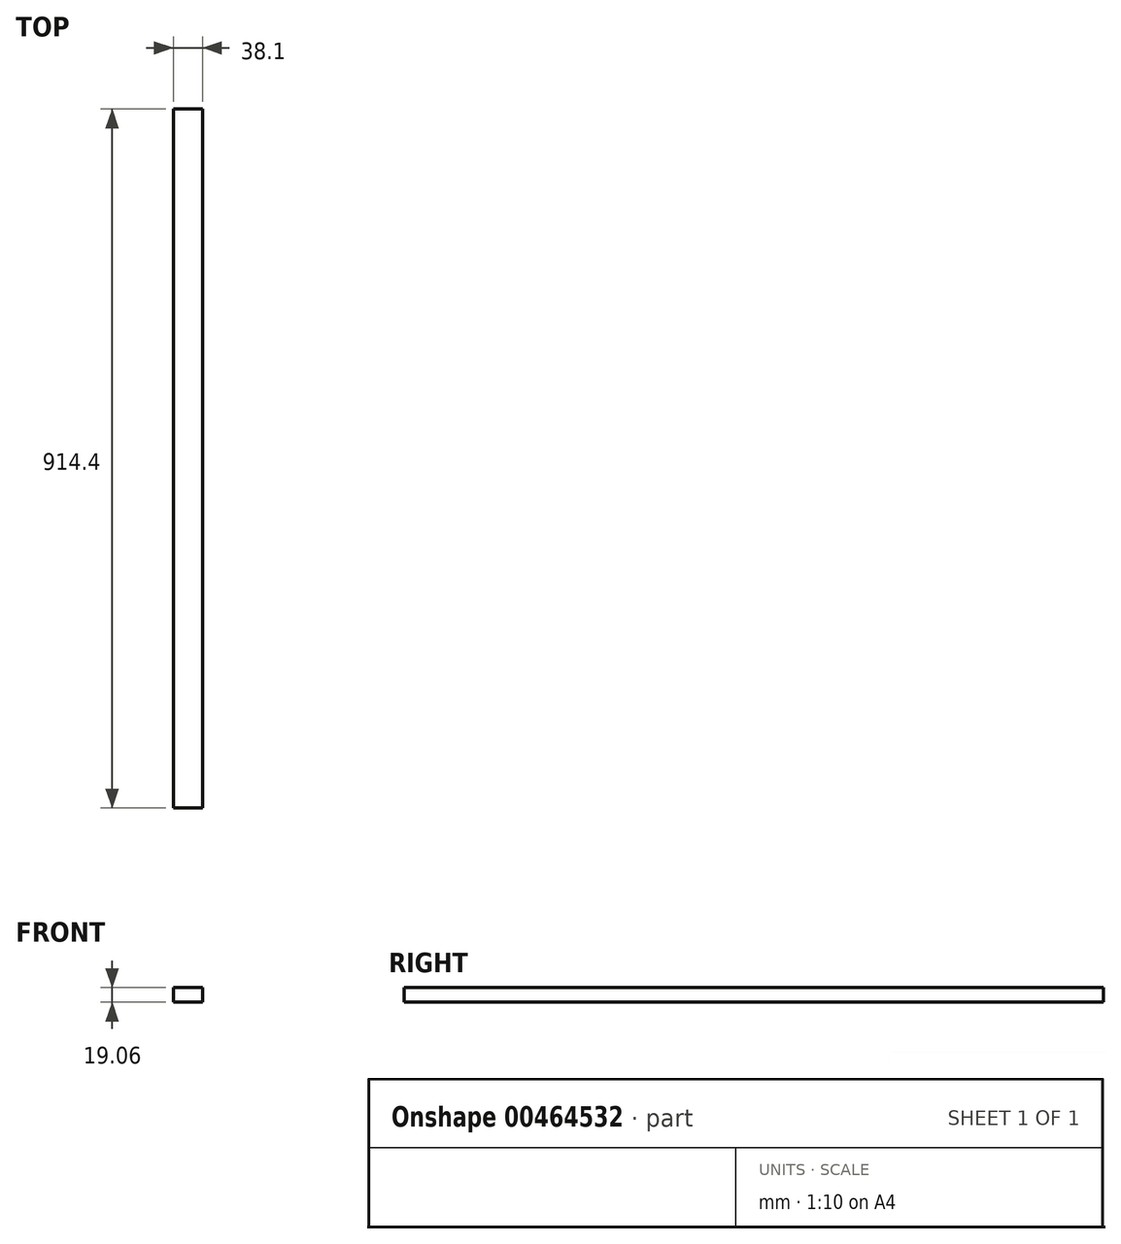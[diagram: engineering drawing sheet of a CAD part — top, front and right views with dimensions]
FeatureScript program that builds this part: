
annotation { "Feature Type Name" : "Feature", "Feature Type Description" : "" }
export const myFeature = defineFeature(function(context is Context, id is Id, definition is map)
    precondition{}
    {
        {
            var Q0;
            Q0=qCreatedBy(makeId("Front.planeOp"),FACE);
            var sketch = newSketch(context, id + "F0", { "sketchPlane" : qUnion([Q0])});
            skLineSegment(sketch, "E0.bottom", {"start": v(19.05, -9.52) * mm, "end": v(-19.05, -9.53) * mm});
            skLineSegment(sketch, "E0.top", {"start": v(19.05, 9.53) * mm, "end": v(-19.05, 9.53) * mm});
            skLineSegment(sketch, "E0.left", {"start": v(19.05, -9.52) * mm, "end": v(19.05, 9.53) * mm});
            skLineSegment(sketch, "E0.right", {"start": v(-19.05, -9.53) * mm, "end": v(-19.05, 9.53) * mm});
            skPoint(sketch, "E0.middle", {"position": v(0, 0) * mm});
            skSolve(sketch);
        }
        {
            var Q0;
            Q0 = qSketchRegion(id + "F0", true);
            extrude(context, id + "F1", {"entities" : qUnion([Q0]), "depth" : 914.4 * mm, "symmetric" : true});
        }
    });
